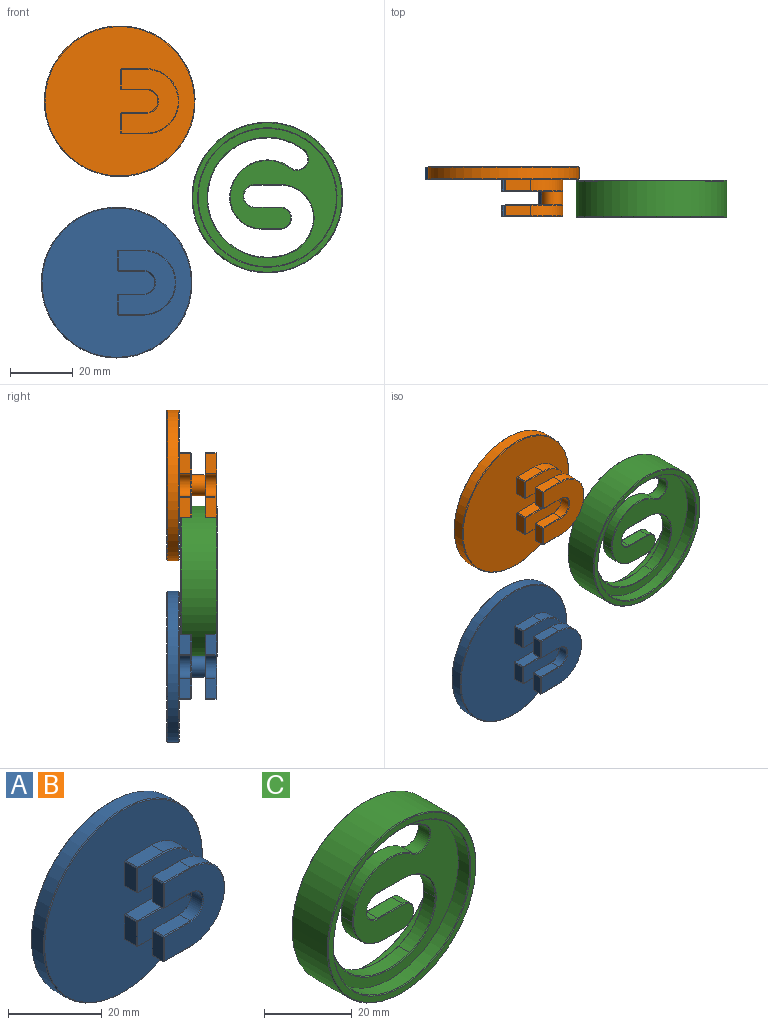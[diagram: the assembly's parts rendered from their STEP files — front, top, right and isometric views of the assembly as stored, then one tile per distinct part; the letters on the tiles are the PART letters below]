
ASSEMBLY  parts=3 mates=2
PART A: 75 faces, bbox 48x15.9x48 mm
  f0: cylinder r=24mm len=48mm, axis (0,-1,0), area 542.9mm2, adj f73,f74
  f1: plane 47.6x47.6mm, normal (0,1,0), area 1779.5mm2, adj f73
  f2: plane 47.6x47.6mm, normal (0,-1,0), area 1522.4mm2, adj f15,f16,f18,f19,f20,f21,f22,f23
  f3: cylinder r=3.35mm len=6.7mm, axis (0,1,0), area 91.7mm2, adj f4,f14,f17,f24,f27,f29,f39,f41
  f4: plane 18.06x9.31mm, normal (0,1,0), area 102.3mm2, adj f3,f46,f51,f57,f66,f69
  f5: cylinder r=3.65mm len=7.3mm, axis (0,1,0), area 37.8mm2, adj f6,f12,f54,f69,f71
  f6: plane 8x3.3mm, normal (0,0,1), area 26.4mm2, adj f5,f59,f67,f72
  f7: plane 6.3x3.3mm, normal (-1,0,0), area 20.8mm2, adj f60,f61,f67,f68
  f8: plane 8x3.3mm, normal (0,0,-1), area 26.4mm2, adj f9,f50,f61,f62
  f9: cylinder r=10.35mm len=20.7mm, axis (0,1,0), area 107.3mm2, adj f8,f10,f45,f51,f56
  f10: plane 8x3.3mm, normal (0,0,1), area 26.4mm2, adj f9,f43,f46,f47
  f11: plane 6.3x3.3mm, normal (-1,0,0), area 20.8mm2, adj f47,f48,f57,f58
  f12: plane 8x3.3mm, normal (0,0,-1), area 26.4mm2, adj f5,f49,f58,f66
  f13: plane 20.3x18.15mm, normal (0,-1,0), area 239.3mm2, adj f43,f45,f48,f49,f50,f54,f59,f60
  f14: plane 18.06x9.31mm, normal (0,1,0), area 102.3mm2, adj f3,f56,f62,f68,f71,f72
  f15: cylinder r=3.65mm len=7.3mm, axis (0,1,0), area 41.9mm2, adj f2,f18,f23,f27,f29
  f16: cylinder r=10.35mm len=20.7mm, axis (0,1,0), area 118.7mm2, adj f2,f20,f21,f39,f41
  f17: plane 18.06x9.31mm, normal (0,-1,0), area 102.3mm2, adj f3,f25,f27,f30,f36,f39
  f18: plane 8x3.65mm, normal (0,0,1), area 29.2mm2, adj f2,f15,f32,f33
  f19: plane 6.3x3.65mm, normal (-1,0,0), area 23mm2, adj f2,f32,f37,f38
  f20: plane 8x3.65mm, normal (0,0,-1), area 29.2mm2, adj f2,f16,f37,f42
  f21: plane 8x3.65mm, normal (0,0,1), area 29.2mm2, adj f2,f16,f31,f36
  f22: plane 6.3x3.65mm, normal (-1,0,0), area 23mm2, adj f2,f26,f30,f31
  f23: plane 8x3.65mm, normal (0,0,-1), area 29.2mm2, adj f2,f15,f25,f26
  f24: plane 18.06x9.31mm, normal (0,-1,0), area 102.3mm2, adj f3,f29,f33,f38,f41,f42
  f25: plane 8x0.2mm, normal (0,-0.71,-0.71), area 2.3mm2, adj f17,f23,f27,f28
  f26: plane 3.65x0.2mm, normal (-0.71,0,-0.71), area 1mm2, adj f2,f22,f23,f28
  f27: cone r=3.65mm half-angle=45deg, axis (0,-1,0), area 1.5mm2, adj f3,f15,f17,f25
  f28: plane 0.2x0.2mm, normal (-0.58,-0.58,-0.58), area 0mm2, adj f25,f26,f30
  f29: cone r=3.65mm half-angle=45deg, axis (0,-1,0), area 1.5mm2, adj f3,f15,f24,f33
  f30: plane 6.3x0.2mm, normal (-0.71,-0.71,0), area 1.8mm2, adj f17,f22,f28,f34
  f31: plane 3.65x0.2mm, normal (-0.71,0,0.71), area 1mm2, adj f2,f21,f22,f34
  f32: plane 3.65x0.2mm, normal (-0.71,0,0.71), area 1mm2, adj f2,f18,f19,f35
  f33: plane 8x0.2mm, normal (0,-0.71,0.71), area 2.3mm2, adj f18,f24,f29,f35
  f34: plane 0.2x0.2mm, normal (-0.58,-0.58,0.58), area 0mm2, adj f30,f31,f36
  f35: plane 0.2x0.2mm, normal (-0.58,-0.58,0.58), area 0mm2, adj f32,f33,f38
  f36: plane 8x0.2mm, normal (0,-0.71,0.71), area 2.3mm2, adj f17,f21,f34,f39
  f37: plane 3.65x0.2mm, normal (-0.71,0,-0.71), area 1mm2, adj f2,f19,f20,f40
  f38: plane 6.3x0.2mm, normal (-0.71,-0.71,0), area 1.8mm2, adj f19,f24,f35,f40
  f39: cone r=10.15mm half-angle=45deg, axis (0,1,0), area 4.3mm2, adj f3,f16,f17,f36
  f40: plane 0.2x0.2mm, normal (-0.58,-0.58,-0.58), area 0mm2, adj f37,f38,f42
  f41: cone r=10.15mm half-angle=45deg, axis (0,1,0), area 4.3mm2, adj f3,f16,f24,f42
  f42: plane 8x0.2mm, normal (0,-0.71,-0.71), area 2.3mm2, adj f20,f24,f40,f41
  f43: plane 8x0.2mm, normal (0,-0.71,0.71), area 2.3mm2, adj f10,f13,f44,f45
  f44: plane 0.2x0.2mm, normal (-0.58,-0.58,0.58), area 0mm2, adj f43,f47,f48
  f45: cone r=10.15mm half-angle=45deg, axis (0,1,0), area 9.1mm2, adj f9,f13,f43,f50
  f46: plane 8x0.2mm, normal (0,0.71,0.71), area 2.3mm2, adj f4,f10,f51,f52
  f47: plane 3.3x0.2mm, normal (-0.71,0,0.71), area 0.9mm2, adj f10,f11,f44,f52
  f48: plane 6.3x0.2mm, normal (-0.71,-0.71,0), area 1.8mm2, adj f11,f13,f44,f53
  f49: plane 8x0.2mm, normal (0,-0.71,-0.71), area 2.3mm2, adj f12,f13,f53,f54
  f50: plane 8x0.2mm, normal (0,-0.71,-0.71), area 2.3mm2, adj f8,f13,f45,f55
  f51: cone r=10.35mm half-angle=45deg, axis (0,-1,0), area 4.3mm2, adj f3,f4,f9,f46
  f52: plane 0.2x0.2mm, normal (-0.58,0.58,0.58), area 0mm2, adj f46,f47,f57
  f53: plane 0.2x0.2mm, normal (-0.58,-0.58,-0.58), area 0mm2, adj f48,f49,f58
  f54: cone r=3.65mm half-angle=45deg, axis (0,-1,0), area 3.3mm2, adj f5,f13,f49,f59
  f55: plane 0.2x0.2mm, normal (-0.58,-0.58,-0.58), area 0mm2, adj f50,f60,f61
  f56: cone r=10.35mm half-angle=45deg, axis (0,-1,0), area 4.3mm2, adj f3,f9,f14,f62
  f57: plane 6.3x0.2mm, normal (-0.71,0.71,0), area 1.8mm2, adj f4,f11,f52,f63
  f58: plane 3.3x0.2mm, normal (-0.71,0,-0.71), area 0.9mm2, adj f11,f12,f53,f63
  f59: plane 8x0.2mm, normal (0,-0.71,0.71), area 2.3mm2, adj f6,f13,f54,f64
  f60: plane 6.3x0.2mm, normal (-0.71,-0.71,0), area 1.8mm2, adj f7,f13,f55,f64
  f61: plane 3.3x0.2mm, normal (-0.71,0,-0.71), area 0.9mm2, adj f7,f8,f55,f65
  f62: plane 8x0.2mm, normal (0,0.71,-0.71), area 2.3mm2, adj f8,f14,f56,f65
  f63: plane 0.2x0.2mm, normal (-0.58,0.58,-0.58), area 0mm2, adj f57,f58,f66
  f64: plane 0.2x0.2mm, normal (-0.58,-0.58,0.58), area 0mm2, adj f59,f60,f67
  f65: plane 0.2x0.2mm, normal (-0.58,0.58,-0.58), area 0mm2, adj f61,f62,f68
  f66: plane 8x0.2mm, normal (0,0.71,-0.71), area 2.3mm2, adj f4,f12,f63,f69
  f67: plane 3.3x0.2mm, normal (-0.71,0,0.71), area 0.9mm2, adj f6,f7,f64,f70
  f68: plane 6.3x0.2mm, normal (-0.71,0.71,0), area 1.8mm2, adj f7,f14,f65,f70
  f69: cone r=3.85mm half-angle=45deg, axis (0,1,0), area 1.5mm2, adj f3,f4,f5,f66
  f70: plane 0.2x0.2mm, normal (-0.58,0.58,0.58), area 0mm2, adj f67,f68,f72
  f71: cone r=3.85mm half-angle=45deg, axis (0,1,0), area 1.5mm2, adj f3,f5,f14,f72
  f72: plane 8x0.2mm, normal (0,0.71,0.71), area 2.3mm2, adj f6,f14,f70,f71
  f73: cone r=24mm half-angle=45deg, axis (0,-1,0), area 42.5mm2, adj f0,f1
  f74: cone r=23.8mm half-angle=45deg, axis (0,1,0), area 42.5mm2, adj f0,f2
PART B: same geometry as A
PART C: 47 faces, bbox 48x11.7x48 mm
  f0: plane 6.2x3.6mm, normal (0,0,-1), area 22.3mm2, adj f1,f16,f18,f29
  f1: cylinder r=3.5mm len=7mm, axis (0,1,0), area 39.6mm2, adj f0,f2,f20,f25
  f2: plane 8.2x3.6mm, normal (0,0,1), area 29.5mm2, adj f1,f3,f22,f28
  f3: cylinder r=3.5mm len=7mm, axis (0,1,0), area 39.6mm2, adj f2,f4,f24,f32
  f4: plane 8.2x3.6mm, normal (0,0,-1), area 29.5mm2, adj f3,f5,f27,f35
  f5: cylinder r=10.5mm len=10.5mm, axis (0,1,0), area 59.4mm2, adj f4,f31,f37,f38
  f6: cylinder r=19mm len=38mm, axis (0,1,0), area 283.3mm2, adj f7,f17,f26,f41
  f7: cylinder r=3.5mm len=6.28mm, axis (0,1,0), area 39.6mm2, adj f6,f8,f23,f39
  f8: cylinder r=12mm len=19.3mm, axis (0,1,0), area 96.9mm2, adj f7,f16,f21,f36
  f9: plane 44x44mm, normal (0,-1,0), area 759.2mm2, adj f12,f25,f28,f29,f32,f33,f35,f36
  f10: plane 44x44mm, normal (0,1,0), area 759.2mm2, adj f11,f18,f19,f20,f21,f22,f23,f24
  f11: cylinder r=22mm len=44mm, axis (0,1,0), area 504.5mm2, adj f10,f44
  f12: cylinder r=22mm len=44mm, axis (0,1,0), area 504.5mm2, adj f9,f46
  f13: cylinder r=24mm len=48mm, axis (0,1,0), area 1704mm2, adj f43,f45
  f14: plane 47.6x47.6mm, normal (0,-1,0), area 231.2mm2, adj f45,f46
  f15: plane 47.6x47.6mm, normal (0,1,0), area 231.2mm2, adj f43,f44
  f16: cylinder r=10mm len=10mm, axis (0,1,0), area 55.9mm2, adj f0,f8,f19,f33
  f17: cylinder r=12.5mm len=11.33mm, axis (0,1,0), area 53.6mm2, adj f6,f30,f37,f42
  f18: plane 6.2x0.2mm, normal (0,0.71,-0.71), area 1.8mm2, adj f0,f10,f19,f20
  f19: cone r=9.8mm half-angle=45deg, axis (0,-1,0), area 4.3mm2, adj f10,f16,f18,f21
  f20: cone r=3.5mm half-angle=45deg, axis (0,-1,0), area 3mm2, adj f1,f10,f18,f22
  f21: cone r=12mm half-angle=45deg, axis (0,-1,0), area 7.6mm2, adj f8,f10,f19,f23
  f22: plane 8.2x0.2mm, normal (0,0.71,0.71), area 2.3mm2, adj f2,f10,f20,f24
  f23: cone r=3.7mm half-angle=45deg, axis (0,1,0), area 3.2mm2, adj f7,f10,f21,f26
  f24: cone r=3.7mm half-angle=45deg, axis (0,1,0), area 3.2mm2, adj f3,f10,f22,f27
  f25: cone r=3.3mm half-angle=45deg, axis (0,1,0), area 3mm2, adj f1,f9,f28,f29
  f26: cone r=19.2mm half-angle=45deg, axis (0,1,0), area 22.4mm2, adj f6,f10,f23,f30
  f27: plane 8.2x0.2mm, normal (0,0.71,-0.71), area 2.3mm2, adj f4,f10,f24,f31
  f28: plane 8.2x0.2mm, normal (0,-0.71,0.71), area 2.3mm2, adj f2,f9,f25,f32
  f29: plane 6.2x0.2mm, normal (0,-0.71,-0.71), area 1.8mm2, adj f0,f9,f25,f33
  f30: cone r=12.7mm half-angle=45deg, axis (0,1,0), area 4.2mm2, adj f10,f17,f26,f34
  f31: cone r=10.7mm half-angle=45deg, axis (0,1,0), area 4.7mm2, adj f5,f10,f27,f34
  f32: cone r=3.5mm half-angle=45deg, axis (0,-1,0), area 3.2mm2, adj f3,f9,f28,f35
  f33: cone r=9.8mm half-angle=45deg, axis (0,1,0), area 4.3mm2, adj f9,f16,f29,f36
  f34: plane 0.2x0.2mm, normal (-0.71,0.71,0.01), area 0mm2, adj f10,f30,f31,f37
  f35: plane 8.2x0.2mm, normal (0,-0.71,-0.71), area 2.3mm2, adj f4,f9,f32,f38
  f36: cone r=11.8mm half-angle=45deg, axis (0,1,0), area 7.6mm2, adj f8,f9,f33,f39
  f37: plane 3.6x0.01mm, normal (-1,0,0.02), area 0mm2, adj f5,f17,f34,f40
  f38: cone r=10.5mm half-angle=45deg, axis (0,-1,0), area 4.7mm2, adj f5,f9,f35,f40
  f39: cone r=3.5mm half-angle=45deg, axis (0,-1,0), area 3.2mm2, adj f7,f9,f36,f41
  f40: plane 0.2x0.2mm, normal (-0.71,-0.71,0.01), area 0mm2, adj f9,f37,f38,f42
  f41: cone r=19mm half-angle=45deg, axis (0,-1,0), area 22.4mm2, adj f6,f9,f39,f42
  f42: cone r=12.7mm half-angle=45deg, axis (0,-1,0), area 4.2mm2, adj f9,f17,f40,f41
  f43: cone r=24mm half-angle=45deg, axis (0,-1,0), area 42.5mm2, adj f13,f15
  f44: cone r=22.2mm half-angle=45deg, axis (0,1,0), area 39.3mm2, adj f11,f15
  f45: cone r=23.8mm half-angle=45deg, axis (0,1,0), area 42.5mm2, adj f13,f14
  f46: cone r=22mm half-angle=45deg, axis (0,-1,0), area 39.3mm2, adj f12,f14
PLACE A t=(-35.42,-41.03,5.66)mm
PLACE B t=(-34.46,-41.03,63.42)mm
PLACE C t=(8.26,-45.18,26.21)mm
MATE planar B.f2 <-> A.f2  axis (0,-1,0) through (-40.36,-41.03,56.88)mm
MATE planar C.f9 <-> B.f4  axis (0,-1,0) through (10.34,-49.18,26.85)mm
